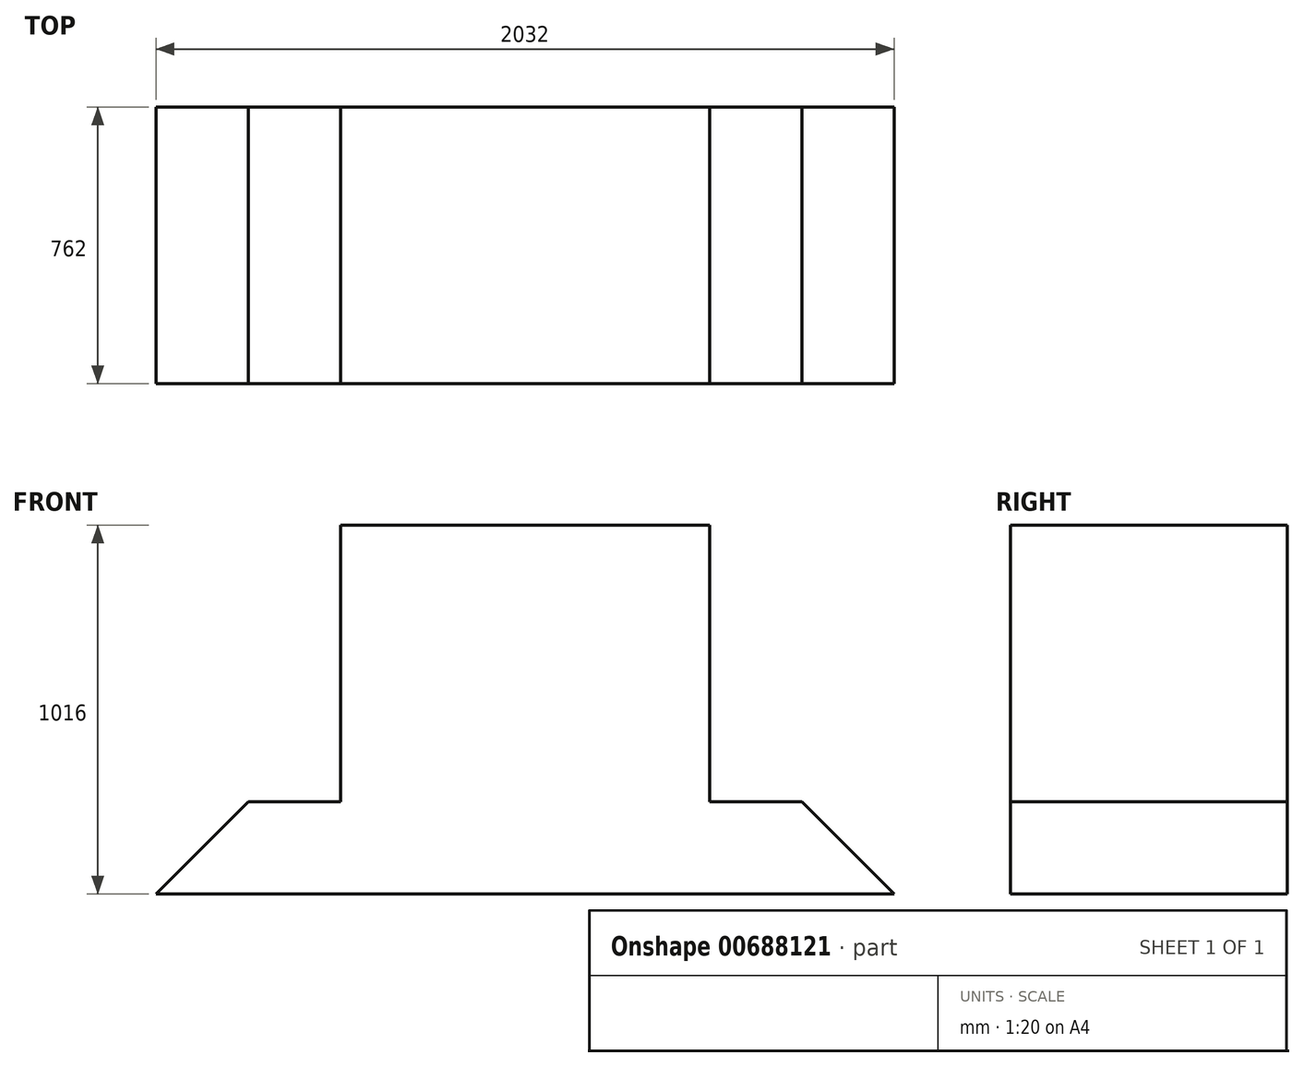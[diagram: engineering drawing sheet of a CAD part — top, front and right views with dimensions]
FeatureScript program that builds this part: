
annotation { "Feature Type Name" : "Feature", "Feature Type Description" : "" }
export const myFeature = defineFeature(function(context is Context, id is Id, definition is map)
    precondition{}
    {
        {
            var Q0;
            Q0=qCreatedBy(makeId("Front.planeOp"),FACE);
            var sketch = newSketch(context, id + "F0", { "sketchPlane" : qUnion([Q0])});
            skLineSegment(sketch, "E0", {"start": v(0, 0) * mm, "end": v(2032, 0) * mm});
            skLineSegment(sketch, "E1", {"start": v(1778, 254) * mm, "end": v(2032, 0) * mm});
            skLineSegment(sketch, "E2", {"start": v(0, 0) * mm, "end": v(254, 254) * mm});
            skLineSegment(sketch, "E3", {"start": v(254, 254) * mm, "end": v(508, 254) * mm});
            skLineSegment(sketch, "E4", {"start": v(508, 254) * mm, "end": v(508, 1016) * mm});
            skLineSegment(sketch, "E5", {"start": v(508, 1016) * mm, "end": v(1524, 1016) * mm});
            skLineSegment(sketch, "E6", {"start": v(1524, 1016) * mm, "end": v(1524, 254) * mm});
            skLineSegment(sketch, "E7", {"start": v(1524, 254) * mm, "end": v(1778, 254) * mm});
            skSolve(sketch);
        }
        {
            var Q0;
            Q0=makeQuery(id+"F0.imprint","IMPRINT",FACE,{"disambiguationData":[TD([[makeQuery(id+"F0.imprint","IMPRINT",EDGE,{"derivedFrom":sQuery(id+"F0.wireOp",EDGE,"E0")}),1.0]])]});
            extrude(context, id + "F1", {"entities" : qUnion([Q0]), "depth" : 762 * mm, "offsetDistance" : 25.4 * mm});
        }
    });
